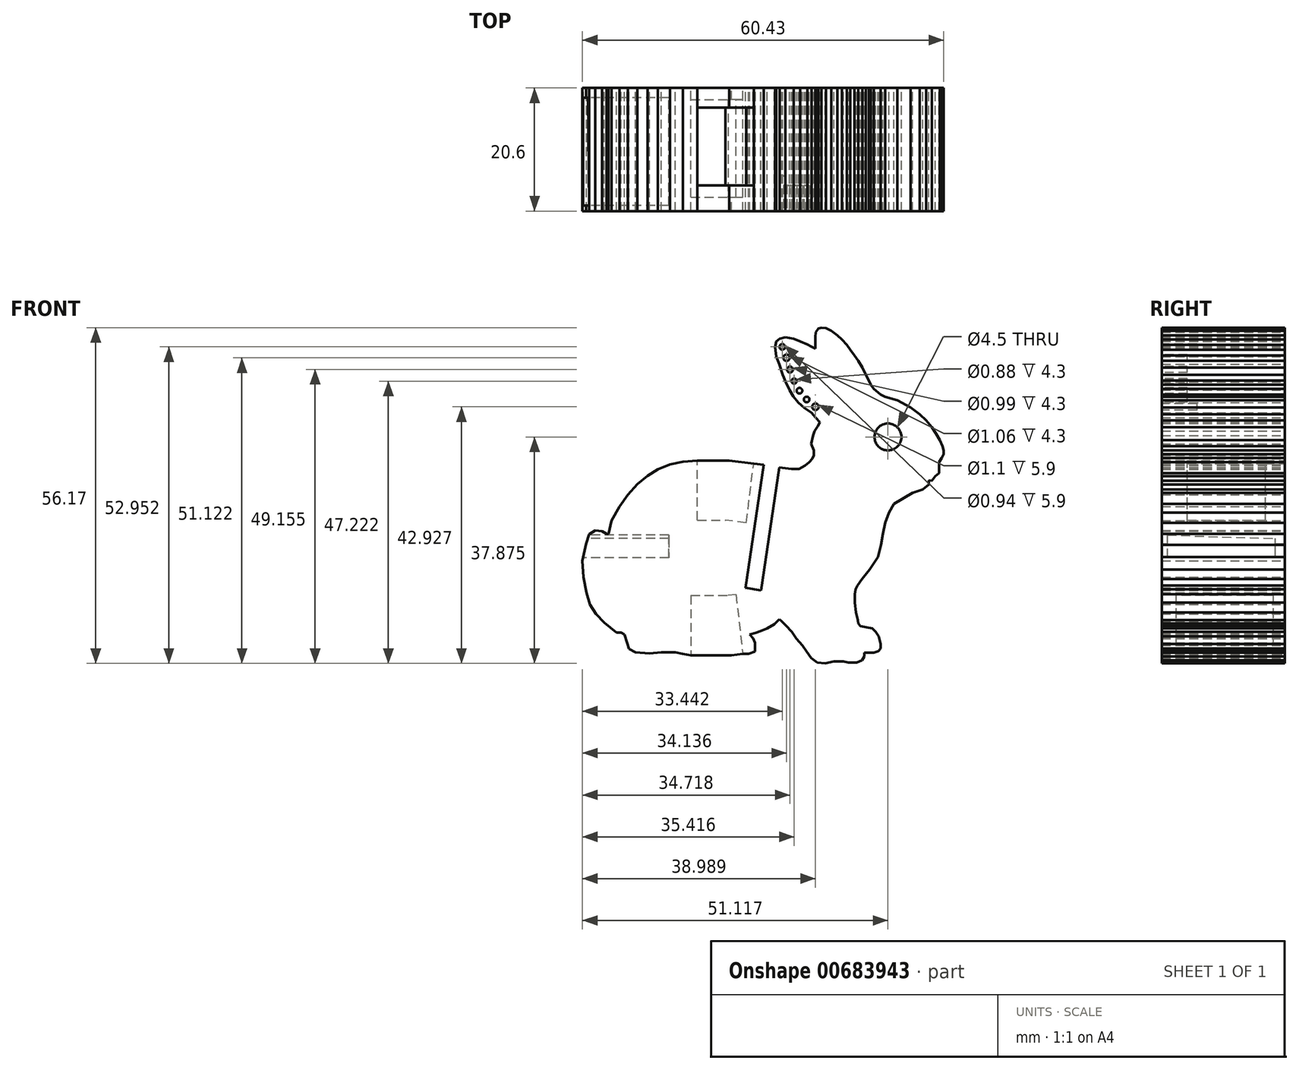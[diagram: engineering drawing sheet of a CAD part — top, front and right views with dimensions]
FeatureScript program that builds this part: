
annotation { "Feature Type Name" : "Feature", "Feature Type Description" : "" }
export const myFeature = defineFeature(function(context is Context, id is Id, definition is map)
    precondition{}
    {
        {
            var Q0;
            Q0=qCreatedBy(makeId("Front.planeOp"),FACE);
            var sketch = newSketch(context, id + "F0", { "sketchPlane" : qUnion([Q0])});
            skLineSegment(sketch, "E0", {"start": v(59.18, 31.9) * mm, "end": v(59.18, 31.2) * mm});
            skLineSegment(sketch, "E1", {"start": v(59.18, 31.2) * mm, "end": v(58.21, 30.37) * mm});
            skLineSegment(sketch, "E2", {"start": v(58.21, 30.37) * mm, "end": v(56.46, 29.85) * mm});
            skLineSegment(sketch, "E3", {"start": v(56.46, 29.85) * mm, "end": v(53.36, 27.96) * mm});
            skLineSegment(sketch, "E4", {"start": v(53.36, 27.96) * mm, "end": v(52.57, 26.52) * mm});
            skLineSegment(sketch, "E5", {"start": v(52.57, 26.52) * mm, "end": v(51.91, 24.8) * mm});
            skLineSegment(sketch, "E6", {"start": v(51.91, 24.8) * mm, "end": v(51.53, 22.99) * mm});
            skLineSegment(sketch, "E7", {"start": v(51.53, 22.99) * mm, "end": v(51.19, 21.11) * mm});
            skLineSegment(sketch, "E8", {"start": v(51.19, 21.11) * mm, "end": v(50.68, 19.1) * mm});
            skLineSegment(sketch, "E9", {"start": v(50.68, 19.1) * mm, "end": v(49.32, 17.01) * mm});
            skLineSegment(sketch, "E10", {"start": v(49.32, 17.01) * mm, "end": v(48.02, 15.39) * mm});
            skLineSegment(sketch, "E11", {"start": v(48.02, 15.39) * mm, "end": v(47.24, 14.33) * mm});
            skLineSegment(sketch, "E12", {"start": v(47.24, 14.33) * mm, "end": v(46.93, 13.71) * mm});
            skLineSegment(sketch, "E13", {"start": v(46.93, 13.71) * mm, "end": v(46.8, 12.88) * mm});
            skLineSegment(sketch, "E14", {"start": v(46.8, 12.88) * mm, "end": v(46.8, 11.49) * mm});
            skLineSegment(sketch, "E15", {"start": v(46.8, 11.49) * mm, "end": v(47.02, 9.82) * mm});
            skLineSegment(sketch, "E16", {"start": v(47.02, 9.82) * mm, "end": v(47.3, 8.54) * mm});
            skLineSegment(sketch, "E17", {"start": v(47.3, 8.54) * mm, "end": v(47.4, 8) * mm});
            skLineSegment(sketch, "E18", {"start": v(47.4, 8) * mm, "end": v(47.8, 7.53) * mm});
            skLineSegment(sketch, "E19", {"start": v(47.8, 7.53) * mm, "end": v(48.73, 7.33) * mm});
            skLineSegment(sketch, "E20", {"start": v(48.73, 7.33) * mm, "end": v(49.72, 7.17) * mm});
            skLineSegment(sketch, "E21", {"start": v(49.72, 7.17) * mm, "end": v(50.33, 6.61) * mm});
            skLineSegment(sketch, "E22", {"start": v(50.33, 6.61) * mm, "end": v(50.85, 5.82) * mm});
            skLineSegment(sketch, "E23", {"start": v(50.85, 5.82) * mm, "end": v(51.16, 4.55) * mm});
            skLineSegment(sketch, "E24", {"start": v(51.16, 4.55) * mm, "end": v(51.16, 3.77) * mm});
            skLineSegment(sketch, "E25", {"start": v(51.16, 3.77) * mm, "end": v(50.77, 3.37) * mm});
            skLineSegment(sketch, "E26", {"start": v(50.77, 3.37) * mm, "end": v(49.97, 3.1) * mm});
            skLineSegment(sketch, "E27", {"start": v(49.97, 3.1) * mm, "end": v(48.4, 3.1) * mm});
            skLineSegment(sketch, "E28", {"start": v(48.4, 3.1) * mm, "end": v(48.4, 2.43) * mm});
            skLineSegment(sketch, "E29", {"start": v(48.4, 2.43) * mm, "end": v(48.04, 1.82) * mm});
            skLineSegment(sketch, "E30", {"start": v(48.04, 1.82) * mm, "end": v(47.14, 1.41) * mm});
            skLineSegment(sketch, "E31", {"start": v(47.14, 1.41) * mm, "end": v(45.74, 1.41) * mm});
            skLineSegment(sketch, "E32", {"start": v(45.74, 1.41) * mm, "end": v(44.91, 1.62) * mm});
            skLineSegment(sketch, "E33", {"start": v(44.91, 1.62) * mm, "end": v(43.35, 1.62) * mm});
            skLineSegment(sketch, "E34", {"start": v(43.35, 1.62) * mm, "end": v(41.85, 1.3) * mm});
            skLineSegment(sketch, "E35", {"start": v(41.85, 1.3) * mm, "end": v(40.56, 1.41) * mm});
            skLineSegment(sketch, "E36", {"start": v(40.56, 1.41) * mm, "end": v(39.54, 2.2) * mm});
            skLineSegment(sketch, "E37", {"start": v(39.54, 2.2) * mm, "end": v(38.77, 3.29) * mm});
            skLineSegment(sketch, "E38", {"start": v(38.77, 3.29) * mm, "end": v(38.07, 4.3) * mm});
            skLineSegment(sketch, "E39", {"start": v(38.07, 4.3) * mm, "end": v(37.07, 5.46) * mm});
            skLineSegment(sketch, "E40", {"start": v(37.07, 5.46) * mm, "end": v(36.3, 6.57) * mm});
            skLineSegment(sketch, "E41", {"start": v(36.3, 6.57) * mm, "end": v(35.28, 7.7) * mm});
            skLineSegment(sketch, "E42", {"start": v(35.28, 7.7) * mm, "end": v(34.6, 8.39) * mm});
            skLineSegment(sketch, "E43", {"start": v(34.6, 8.39) * mm, "end": v(34.18, 8.68) * mm});
            skLineSegment(sketch, "E44", {"start": v(34.18, 8.68) * mm, "end": v(33.34, 7.84) * mm});
            skLineSegment(sketch, "E45", {"start": v(33.34, 7.84) * mm, "end": v(32.19, 7.18) * mm});
            skLineSegment(sketch, "E46", {"start": v(32.19, 7.18) * mm, "end": v(31.1, 6.72) * mm});
            skLineSegment(sketch, "E47", {"start": v(31.1, 6.72) * mm, "end": v(30.18, 6.39) * mm});
            skLineSegment(sketch, "E48", {"start": v(30.18, 6.39) * mm, "end": v(29.26, 6.12) * mm});
            skLineSegment(sketch, "E49", {"start": v(29.26, 6.12) * mm, "end": v(29.8, 5.51) * mm});
            skLineSegment(sketch, "E50", {"start": v(29.8, 5.51) * mm, "end": v(30.13, 4.73) * mm});
            skLineSegment(sketch, "E51", {"start": v(30.13, 4.73) * mm, "end": v(30.13, 4.07) * mm});
            skLineSegment(sketch, "E52", {"start": v(30.13, 4.07) * mm, "end": v(30.13, 3.51) * mm});
            skLineSegment(sketch, "E53", {"start": v(30.13, 3.51) * mm, "end": v(30.13, 3.29) * mm});
            skLineSegment(sketch, "E54", {"start": v(30.13, 3.29) * mm, "end": v(29.07, 2.88) * mm});
            skLineSegment(sketch, "E55", {"start": v(29.07, 2.88) * mm, "end": v(28.07, 2.88) * mm});
            skLineSegment(sketch, "E56", {"start": v(28.07, 2.88) * mm, "end": v(26.19, 2.66) * mm});
            skLineSegment(sketch, "E57", {"start": v(26.19, 2.66) * mm, "end": v(23.74, 2.66) * mm});
            skLineSegment(sketch, "E58", {"start": v(23.74, 2.66) * mm, "end": v(21.88, 2.66) * mm});
            skLineSegment(sketch, "E59", {"start": v(21.88, 2.66) * mm, "end": v(19.4, 2.66) * mm});
            skLineSegment(sketch, "E60", {"start": v(19.4, 2.66) * mm, "end": v(18, 2.88) * mm});
            skLineSegment(sketch, "E61", {"start": v(18, 2.88) * mm, "end": v(16.82, 3.14) * mm});
            skLineSegment(sketch, "E62", {"start": v(16.82, 3.14) * mm, "end": v(14.45, 3.14) * mm});
            skLineSegment(sketch, "E63", {"start": v(14.45, 3.14) * mm, "end": v(12.45, 3) * mm});
            skLineSegment(sketch, "E64", {"start": v(12.45, 3) * mm, "end": v(10.14, 3.13) * mm});
            skLineSegment(sketch, "E65", {"start": v(10.14, 3.13) * mm, "end": v(9.06, 3.73) * mm});
            skLineSegment(sketch, "E66", {"start": v(9.06, 3.73) * mm, "end": v(8.7, 4.73) * mm});
            skLineSegment(sketch, "E67", {"start": v(8.7, 4.73) * mm, "end": v(8.3, 6.14) * mm});
            skLineSegment(sketch, "E68", {"start": v(8.3, 6.14) * mm, "end": v(7.74, 6.47) * mm});
            skLineSegment(sketch, "E69", {"start": v(7.74, 6.47) * mm, "end": v(6.93, 6.47) * mm});
            skLineSegment(sketch, "E70", {"start": v(6.93, 6.47) * mm, "end": v(4.9, 8.14) * mm});
            skLineSegment(sketch, "E71", {"start": v(4.9, 8.14) * mm, "end": v(3.53, 9.54) * mm});
            skLineSegment(sketch, "E72", {"start": v(3.53, 9.54) * mm, "end": v(2.47, 11.15) * mm});
            skLineSegment(sketch, "E73", {"start": v(2.47, 11.15) * mm, "end": v(1.9, 13.14) * mm});
            skLineSegment(sketch, "E74", {"start": v(1.9, 13.14) * mm, "end": v(1.4, 15.75) * mm});
            skLineSegment(sketch, "E75", {"start": v(1.4, 15.75) * mm, "end": v(1.25, 18.43) * mm});
            skLineSegment(sketch, "E76", {"start": v(1.25, 18.43) * mm, "end": v(1.86, 21.3) * mm});
            skLineSegment(sketch, "E77", {"start": v(1.86, 21.3) * mm, "end": v(2.39, 22.87) * mm});
            skLineSegment(sketch, "E78", {"start": v(2.39, 22.87) * mm, "end": v(3.37, 23.56) * mm});
            skLineSegment(sketch, "E79", {"start": v(3.37, 23.56) * mm, "end": v(4.55, 23.4) * mm});
            skLineSegment(sketch, "E80", {"start": v(4.55, 23.4) * mm, "end": v(5.28, 22.99) * mm});
            skLineSegment(sketch, "E81", {"start": v(5.28, 22.99) * mm, "end": v(5.63, 22.99) * mm});
            skLineSegment(sketch, "E82", {"start": v(5.63, 22.99) * mm, "end": v(6.1, 25.22) * mm});
            skLineSegment(sketch, "E83", {"start": v(6.1, 25.22) * mm, "end": v(7.44, 27.53) * mm});
            skLineSegment(sketch, "E84", {"start": v(7.44, 27.53) * mm, "end": v(8.84, 29.53) * mm});
            skLineSegment(sketch, "E85", {"start": v(8.84, 29.53) * mm, "end": v(10.46, 31.27) * mm});
            skLineSegment(sketch, "E86", {"start": v(10.46, 31.27) * mm, "end": v(12.13, 32.66) * mm});
            skLineSegment(sketch, "E87", {"start": v(12.13, 32.66) * mm, "end": v(13.85, 33.74) * mm});
            skLineSegment(sketch, "E88", {"start": v(13.85, 33.74) * mm, "end": v(15.89, 34.56) * mm});
            skLineSegment(sketch, "E89", {"start": v(15.89, 34.56) * mm, "end": v(18.07, 35.02) * mm});
            skLineSegment(sketch, "E90", {"start": v(18.07, 35.02) * mm, "end": v(20.5, 35.25) * mm});
            skLineSegment(sketch, "E91", {"start": v(20.5, 35.25) * mm, "end": v(22.93, 35.25) * mm});
            skLineSegment(sketch, "E92", {"start": v(22.93, 35.25) * mm, "end": v(25.8, 35.25) * mm});
            skLineSegment(sketch, "E93", {"start": v(25.8, 35.25) * mm, "end": v(29.9, 34.74) * mm});
            skLineSegment(sketch, "E94", {"start": v(29.9, 34.74) * mm, "end": v(31.58, 34.5) * mm});
            skLineSegment(sketch, "E95", {"start": v(31.58, 34.5) * mm, "end": v(34.17, 34.11) * mm});
            skLineSegment(sketch, "E96", {"start": v(34.17, 34.11) * mm, "end": v(36.24, 33.84) * mm});
            skLineSegment(sketch, "E97", {"start": v(36.24, 33.84) * mm, "end": v(37.5, 33.84) * mm});
            skLineSegment(sketch, "E98", {"start": v(37.5, 33.84) * mm, "end": v(38.48, 34.41) * mm});
            skLineSegment(sketch, "E99", {"start": v(38.48, 34.41) * mm, "end": v(39.21, 34.95) * mm});
            skLineSegment(sketch, "E100", {"start": v(39.21, 34.95) * mm, "end": v(39.69, 35.51) * mm});
            skLineSegment(sketch, "E101", {"start": v(39.69, 35.51) * mm, "end": v(39.94, 36.1) * mm});
            skLineSegment(sketch, "E102", {"start": v(39.94, 36.1) * mm, "end": v(39.94, 36.93) * mm});
            skLineSegment(sketch, "E103", {"start": v(39.94, 36.93) * mm, "end": v(39.54, 38.02) * mm});
            skLineSegment(sketch, "E104", {"start": v(39.54, 38.02) * mm, "end": v(39.83, 39.44) * mm});
            skLineSegment(sketch, "E105", {"start": v(39.83, 39.44) * mm, "end": v(40.08, 40.2) * mm});
            skLineSegment(sketch, "E106", {"start": v(40.08, 40.2) * mm, "end": v(40.6, 40.94) * mm});
            skLineSegment(sketch, "E107", {"start": v(40.6, 40.94) * mm, "end": v(41, 41.61) * mm});
            skLineSegment(sketch, "E108", {"start": v(41, 41.61) * mm, "end": v(40.3, 42.4) * mm});
            skLineSegment(sketch, "E109", {"start": v(40.3, 42.4) * mm, "end": v(39.57, 43.22) * mm});
            skLineSegment(sketch, "E110", {"start": v(39.57, 43.22) * mm, "end": v(38.4, 44.03) * mm});
            skLineSegment(sketch, "E111", {"start": v(38.4, 44.03) * mm, "end": v(37.38, 44.92) * mm});
            skLineSegment(sketch, "E112", {"start": v(37.38, 44.92) * mm, "end": v(36.53, 45.97) * mm});
            skLineSegment(sketch, "E113", {"start": v(36.53, 45.97) * mm, "end": v(35.9, 47.05) * mm});
            skLineSegment(sketch, "E114", {"start": v(35.9, 47.05) * mm, "end": v(35.26, 48.39) * mm});
            skLineSegment(sketch, "E115", {"start": v(35.26, 48.39) * mm, "end": v(34.77, 49.59) * mm});
            skLineSegment(sketch, "E116", {"start": v(34.77, 49.59) * mm, "end": v(34.17, 51.34) * mm});
            skLineSegment(sketch, "E117", {"start": v(34.17, 51.34) * mm, "end": v(33.68, 52.6) * mm});
            skLineSegment(sketch, "E118", {"start": v(33.68, 52.6) * mm, "end": v(33.5, 54.23) * mm});
            skLineSegment(sketch, "E119", {"start": v(33.5, 54.23) * mm, "end": v(33.67, 55.17) * mm});
            skLineSegment(sketch, "E120", {"start": v(33.67, 55.17) * mm, "end": v(34.28, 55.63) * mm});
            skLineSegment(sketch, "E121", {"start": v(34.28, 55.63) * mm, "end": v(35.19, 55.89) * mm});
            skLineSegment(sketch, "E122", {"start": v(35.19, 55.89) * mm, "end": v(36.57, 55.6) * mm});
            skLineSegment(sketch, "E123", {"start": v(36.57, 55.6) * mm, "end": v(37.7, 55.18) * mm});
            skLineSegment(sketch, "E124", {"start": v(37.7, 55.18) * mm, "end": v(38.87, 54.67) * mm});
            skLineSegment(sketch, "E125", {"start": v(38.87, 54.67) * mm, "end": v(39.6, 54.27) * mm});
            skLineSegment(sketch, "E126", {"start": v(39.6, 54.27) * mm, "end": v(40.2, 53.98) * mm});
            skLineSegment(sketch, "E127", {"start": v(40.2, 53.98) * mm, "end": v(40.2, 55.95) * mm});
            skLineSegment(sketch, "E128", {"start": v(40.2, 55.95) * mm, "end": v(40.3, 56.68) * mm});
            skLineSegment(sketch, "E129", {"start": v(40.3, 56.68) * mm, "end": v(40.7, 57.32) * mm});
            skLineSegment(sketch, "E130", {"start": v(40.7, 57.32) * mm, "end": v(41.2, 57.47) * mm});
            skLineSegment(sketch, "E131", {"start": v(41.2, 57.47) * mm, "end": v(41.98, 57.38) * mm});
            skLineSegment(sketch, "E132", {"start": v(41.98, 57.38) * mm, "end": v(42.9, 56.96) * mm});
            skLineSegment(sketch, "E133", {"start": v(42.9, 56.96) * mm, "end": v(43.88, 56.18) * mm});
            skLineSegment(sketch, "E134", {"start": v(43.88, 56.18) * mm, "end": v(44.66, 55.47) * mm});
            skLineSegment(sketch, "E135", {"start": v(44.66, 55.47) * mm, "end": v(45.46, 54.57) * mm});
            skLineSegment(sketch, "E136", {"start": v(45.46, 54.57) * mm, "end": v(46.07, 53.8) * mm});
            skLineSegment(sketch, "E137", {"start": v(46.07, 53.8) * mm, "end": v(46.74, 52.83) * mm});
            skLineSegment(sketch, "E138", {"start": v(46.74, 52.83) * mm, "end": v(47.4, 51.92) * mm});
            skLineSegment(sketch, "E139", {"start": v(47.4, 51.92) * mm, "end": v(48.07, 50.76) * mm});
            skLineSegment(sketch, "E140", {"start": v(48.07, 50.76) * mm, "end": v(48.69, 49.58) * mm});
            skLineSegment(sketch, "E141", {"start": v(48.69, 49.58) * mm, "end": v(49.16, 48.64) * mm});
            skLineSegment(sketch, "E142", {"start": v(49.16, 48.64) * mm, "end": v(49.5, 47.92) * mm});
            skLineSegment(sketch, "E143", {"start": v(49.5, 47.92) * mm, "end": v(50.03, 47.25) * mm});
            skLineSegment(sketch, "E144", {"start": v(50.03, 47.25) * mm, "end": v(51.16, 46.28) * mm});
            skLineSegment(sketch, "E145", {"start": v(51.16, 46.28) * mm, "end": v(51.87, 45.89) * mm});
            skLineSegment(sketch, "E146", {"start": v(51.87, 45.89) * mm, "end": v(53.94, 45.3) * mm});
            skLineSegment(sketch, "E147", {"start": v(53.94, 45.3) * mm, "end": v(56.13, 44.1) * mm});
            skLineSegment(sketch, "E148", {"start": v(56.13, 44.1) * mm, "end": v(57.69, 42.96) * mm});
            skLineSegment(sketch, "E149", {"start": v(57.69, 42.96) * mm, "end": v(58.76, 41.92) * mm});
            skLineSegment(sketch, "E150", {"start": v(58.76, 41.92) * mm, "end": v(59.7, 40.84) * mm});
            skLineSegment(sketch, "E151", {"start": v(59.7, 40.84) * mm, "end": v(60.39, 39.73) * mm});
            skLineSegment(sketch, "E152", {"start": v(60.39, 39.73) * mm, "end": v(61.06, 38.64) * mm});
            skLineSegment(sketch, "E153", {"start": v(61.06, 38.64) * mm, "end": v(61.48, 37.65) * mm});
            skLineSegment(sketch, "E154", {"start": v(61.48, 37.65) * mm, "end": v(61.68, 36.96) * mm});
            skLineSegment(sketch, "E155", {"start": v(61.68, 36.96) * mm, "end": v(61.68, 36.3) * mm});
            skLineSegment(sketch, "E156", {"start": v(61.68, 36.3) * mm, "end": v(61.36, 35.64) * mm});
            skLineSegment(sketch, "E157", {"start": v(61.36, 35.64) * mm, "end": v(60.9, 34.95) * mm});
            skLineSegment(sketch, "E158", {"start": v(60.9, 34.95) * mm, "end": v(60.9, 33.94) * mm});
            skLineSegment(sketch, "E159", {"start": v(60.9, 33.94) * mm, "end": v(60.9, 33.16) * mm});
            skLineSegment(sketch, "E160", {"start": v(60.9, 33.16) * mm, "end": v(60.3, 32.6) * mm});
            skLineSegment(sketch, "E161", {"start": v(60.3, 32.6) * mm, "end": v(59.74, 31.88) * mm});
            skLineSegment(sketch, "E162", {"start": v(59.74, 31.88) * mm, "end": v(59.18, 31.9) * mm});
            skCircle(sketch, "E163", {"center": v(52.37, 39.17) * mm, "radius": 2.25 * mm});
            skSolve(sketch);
        }
        {
            var Q0;
            Q0=makeQuery(id+"F0.imprint","IMPRINT",FACE,{"disambiguationData":[TD([[makeQuery(id+"F0.imprint","IMPRINT",EDGE,{"derivedFrom":sQuery(id+"F0.wireOp",EDGE,"E0")}),-1.0]])]});
            extrude(context, id + "F1", {"entities" : qUnion([Q0]), "depth" : 3 * mm, "offsetDistance" : 25 * mm});
        }
        {
            var Q0;
            Q0=makeQuery(id+"F1.opExtrude","CAP_FACE",FACE,{"disambiguationData":[OSD([sQuery(id+"F0.wireOp",EDGE,"E0"),sQuery(id+"F0.wireOp",EDGE,"E1"),sQuery(id+"F0.wireOp",EDGE,"E2"),sQuery(id+"F0.wireOp",EDGE,"E3"),sQuery(id+"F0.wireOp",EDGE,"E4"),sQuery(id+"F0.wireOp",EDGE,"E5"),sQuery(id+"F0.wireOp",EDGE,"E6"),sQuery(id+"F0.wireOp",EDGE,"E7"),sQuery(id+"F0.wireOp",EDGE,"E8"),sQuery(id+"F0.wireOp",EDGE,"E9"),sQuery(id+"F0.wireOp",EDGE,"E10"),sQuery(id+"F0.wireOp",EDGE,"E11"),sQuery(id+"F0.wireOp",EDGE,"E12"),sQuery(id+"F0.wireOp",EDGE,"E13"),sQuery(id+"F0.wireOp",EDGE,"E14"),sQuery(id+"F0.wireOp",EDGE,"E15"),sQuery(id+"F0.wireOp",EDGE,"E16"),sQuery(id+"F0.wireOp",EDGE,"E17"),sQuery(id+"F0.wireOp",EDGE,"E18"),sQuery(id+"F0.wireOp",EDGE,"E19"),sQuery(id+"F0.wireOp",EDGE,"E20"),sQuery(id+"F0.wireOp",EDGE,"E21"),sQuery(id+"F0.wireOp",EDGE,"E22"),sQuery(id+"F0.wireOp",EDGE,"E23"),sQuery(id+"F0.wireOp",EDGE,"E24"),sQuery(id+"F0.wireOp",EDGE,"E25"),sQuery(id+"F0.wireOp",EDGE,"E26"),sQuery(id+"F0.wireOp",EDGE,"E27"),sQuery(id+"F0.wireOp",EDGE,"E28"),sQuery(id+"F0.wireOp",EDGE,"E29"),sQuery(id+"F0.wireOp",EDGE,"E30"),sQuery(id+"F0.wireOp",EDGE,"E31"),sQuery(id+"F0.wireOp",EDGE,"E32"),sQuery(id+"F0.wireOp",EDGE,"E33"),sQuery(id+"F0.wireOp",EDGE,"E34"),sQuery(id+"F0.wireOp",EDGE,"E35"),sQuery(id+"F0.wireOp",EDGE,"E36"),sQuery(id+"F0.wireOp",EDGE,"E37"),sQuery(id+"F0.wireOp",EDGE,"E38"),sQuery(id+"F0.wireOp",EDGE,"E39"),sQuery(id+"F0.wireOp",EDGE,"E40"),sQuery(id+"F0.wireOp",EDGE,"E41"),sQuery(id+"F0.wireOp",EDGE,"E42"),sQuery(id+"F0.wireOp",EDGE,"E43"),sQuery(id+"F0.wireOp",EDGE,"E44"),sQuery(id+"F0.wireOp",EDGE,"E45"),sQuery(id+"F0.wireOp",EDGE,"E46"),sQuery(id+"F0.wireOp",EDGE,"E47"),sQuery(id+"F0.wireOp",EDGE,"E48"),sQuery(id+"F0.wireOp",EDGE,"E49"),sQuery(id+"F0.wireOp",EDGE,"E50"),sQuery(id+"F0.wireOp",EDGE,"E51"),sQuery(id+"F0.wireOp",EDGE,"E52"),sQuery(id+"F0.wireOp",EDGE,"E53"),sQuery(id+"F0.wireOp",EDGE,"E54"),sQuery(id+"F0.wireOp",EDGE,"E55"),sQuery(id+"F0.wireOp",EDGE,"E56"),sQuery(id+"F0.wireOp",EDGE,"E57"),sQuery(id+"F0.wireOp",EDGE,"E58"),sQuery(id+"F0.wireOp",EDGE,"E59"),sQuery(id+"F0.wireOp",EDGE,"E60"),sQuery(id+"F0.wireOp",EDGE,"E61"),sQuery(id+"F0.wireOp",EDGE,"E62"),sQuery(id+"F0.wireOp",EDGE,"E63"),sQuery(id+"F0.wireOp",EDGE,"E64"),sQuery(id+"F0.wireOp",EDGE,"E65"),sQuery(id+"F0.wireOp",EDGE,"E66"),sQuery(id+"F0.wireOp",EDGE,"E67"),sQuery(id+"F0.wireOp",EDGE,"E68"),sQuery(id+"F0.wireOp",EDGE,"E69"),sQuery(id+"F0.wireOp",EDGE,"E70"),sQuery(id+"F0.wireOp",EDGE,"E71"),sQuery(id+"F0.wireOp",EDGE,"E72"),sQuery(id+"F0.wireOp",EDGE,"E73"),sQuery(id+"F0.wireOp",EDGE,"E74"),sQuery(id+"F0.wireOp",EDGE,"E75"),sQuery(id+"F0.wireOp",EDGE,"E76"),sQuery(id+"F0.wireOp",EDGE,"E77"),sQuery(id+"F0.wireOp",EDGE,"E78"),sQuery(id+"F0.wireOp",EDGE,"E79"),sQuery(id+"F0.wireOp",EDGE,"E80"),sQuery(id+"F0.wireOp",EDGE,"E81"),sQuery(id+"F0.wireOp",EDGE,"E82"),sQuery(id+"F0.wireOp",EDGE,"E83"),sQuery(id+"F0.wireOp",EDGE,"E84"),sQuery(id+"F0.wireOp",EDGE,"E85"),sQuery(id+"F0.wireOp",EDGE,"E86"),sQuery(id+"F0.wireOp",EDGE,"E87"),sQuery(id+"F0.wireOp",EDGE,"E88"),sQuery(id+"F0.wireOp",EDGE,"E89"),sQuery(id+"F0.wireOp",EDGE,"E90"),sQuery(id+"F0.wireOp",EDGE,"E91"),sQuery(id+"F0.wireOp",EDGE,"E92"),sQuery(id+"F0.wireOp",EDGE,"E93"),sQuery(id+"F0.wireOp",EDGE,"E94"),sQuery(id+"F0.wireOp",EDGE,"E95"),sQuery(id+"F0.wireOp",EDGE,"E96"),sQuery(id+"F0.wireOp",EDGE,"E97"),sQuery(id+"F0.wireOp",EDGE,"E98"),sQuery(id+"F0.wireOp",EDGE,"E99"),sQuery(id+"F0.wireOp",EDGE,"E100"),sQuery(id+"F0.wireOp",EDGE,"E101"),sQuery(id+"F0.wireOp",EDGE,"E102"),sQuery(id+"F0.wireOp",EDGE,"E103"),sQuery(id+"F0.wireOp",EDGE,"E104"),sQuery(id+"F0.wireOp",EDGE,"E105"),sQuery(id+"F0.wireOp",EDGE,"E106"),sQuery(id+"F0.wireOp",EDGE,"E107"),sQuery(id+"F0.wireOp",EDGE,"E108"),sQuery(id+"F0.wireOp",EDGE,"E109"),sQuery(id+"F0.wireOp",EDGE,"E110"),sQuery(id+"F0.wireOp",EDGE,"E111"),sQuery(id+"F0.wireOp",EDGE,"E112"),sQuery(id+"F0.wireOp",EDGE,"E113"),sQuery(id+"F0.wireOp",EDGE,"E114"),sQuery(id+"F0.wireOp",EDGE,"E115"),sQuery(id+"F0.wireOp",EDGE,"E116"),sQuery(id+"F0.wireOp",EDGE,"E117"),sQuery(id+"F0.wireOp",EDGE,"E118"),sQuery(id+"F0.wireOp",EDGE,"E119"),sQuery(id+"F0.wireOp",EDGE,"E120"),sQuery(id+"F0.wireOp",EDGE,"E121"),sQuery(id+"F0.wireOp",EDGE,"E122"),sQuery(id+"F0.wireOp",EDGE,"E123"),sQuery(id+"F0.wireOp",EDGE,"E124"),sQuery(id+"F0.wireOp",EDGE,"E125"),sQuery(id+"F0.wireOp",EDGE,"E126"),sQuery(id+"F0.wireOp",EDGE,"E127"),sQuery(id+"F0.wireOp",EDGE,"E128"),sQuery(id+"F0.wireOp",EDGE,"E129"),sQuery(id+"F0.wireOp",EDGE,"E130"),sQuery(id+"F0.wireOp",EDGE,"E131"),sQuery(id+"F0.wireOp",EDGE,"E132"),sQuery(id+"F0.wireOp",EDGE,"E133"),sQuery(id+"F0.wireOp",EDGE,"E134"),sQuery(id+"F0.wireOp",EDGE,"E135"),sQuery(id+"F0.wireOp",EDGE,"E136"),sQuery(id+"F0.wireOp",EDGE,"E137"),sQuery(id+"F0.wireOp",EDGE,"E138"),sQuery(id+"F0.wireOp",EDGE,"E139"),sQuery(id+"F0.wireOp",EDGE,"E140"),sQuery(id+"F0.wireOp",EDGE,"E141"),sQuery(id+"F0.wireOp",EDGE,"E142"),sQuery(id+"F0.wireOp",EDGE,"E143"),sQuery(id+"F0.wireOp",EDGE,"E144"),sQuery(id+"F0.wireOp",EDGE,"E145"),sQuery(id+"F0.wireOp",EDGE,"E146"),sQuery(id+"F0.wireOp",EDGE,"E147"),sQuery(id+"F0.wireOp",EDGE,"E148"),sQuery(id+"F0.wireOp",EDGE,"E149"),sQuery(id+"F0.wireOp",EDGE,"E150"),sQuery(id+"F0.wireOp",EDGE,"E151"),sQuery(id+"F0.wireOp",EDGE,"E152"),sQuery(id+"F0.wireOp",EDGE,"E153"),sQuery(id+"F0.wireOp",EDGE,"E154"),sQuery(id+"F0.wireOp",EDGE,"E155"),sQuery(id+"F0.wireOp",EDGE,"E156"),sQuery(id+"F0.wireOp",EDGE,"E157"),sQuery(id+"F0.wireOp",EDGE,"E158"),sQuery(id+"F0.wireOp",EDGE,"E159"),sQuery(id+"F0.wireOp",EDGE,"E160"),sQuery(id+"F0.wireOp",EDGE,"E161"),sQuery(id+"F0.wireOp",EDGE,"E162"),sQuery(id+"F0.wireOp",EDGE,"E163")])],"isStart":false});
            extrude(context, id + "F2", {"entities" : qUnion([Q0]), "operationType" : NewBodyOperationType.ADD, "depth" : 17.6 * mm, "offsetDistance" : 25 * mm});
        }
        {
            var Q0;
            Q0=makeQuery(id+"F2.opExtrude","CAP_FACE",FACE,{"disambiguationData":[OSD([sQuery(id+"F0.wireOp",EDGE,"E0"),sQuery(id+"F0.wireOp",EDGE,"E1"),sQuery(id+"F0.wireOp",EDGE,"E2"),sQuery(id+"F0.wireOp",EDGE,"E3"),sQuery(id+"F0.wireOp",EDGE,"E4"),sQuery(id+"F0.wireOp",EDGE,"E5"),sQuery(id+"F0.wireOp",EDGE,"E6"),sQuery(id+"F0.wireOp",EDGE,"E7"),sQuery(id+"F0.wireOp",EDGE,"E8"),sQuery(id+"F0.wireOp",EDGE,"E9"),sQuery(id+"F0.wireOp",EDGE,"E10"),sQuery(id+"F0.wireOp",EDGE,"E11"),sQuery(id+"F0.wireOp",EDGE,"E12"),sQuery(id+"F0.wireOp",EDGE,"E13"),sQuery(id+"F0.wireOp",EDGE,"E14"),sQuery(id+"F0.wireOp",EDGE,"E15"),sQuery(id+"F0.wireOp",EDGE,"E16"),sQuery(id+"F0.wireOp",EDGE,"E17"),sQuery(id+"F0.wireOp",EDGE,"E18"),sQuery(id+"F0.wireOp",EDGE,"E19"),sQuery(id+"F0.wireOp",EDGE,"E20"),sQuery(id+"F0.wireOp",EDGE,"E21"),sQuery(id+"F0.wireOp",EDGE,"E22"),sQuery(id+"F0.wireOp",EDGE,"E23"),sQuery(id+"F0.wireOp",EDGE,"E24"),sQuery(id+"F0.wireOp",EDGE,"E25"),sQuery(id+"F0.wireOp",EDGE,"E26"),sQuery(id+"F0.wireOp",EDGE,"E27"),sQuery(id+"F0.wireOp",EDGE,"E28"),sQuery(id+"F0.wireOp",EDGE,"E29"),sQuery(id+"F0.wireOp",EDGE,"E30"),sQuery(id+"F0.wireOp",EDGE,"E31"),sQuery(id+"F0.wireOp",EDGE,"E32"),sQuery(id+"F0.wireOp",EDGE,"E33"),sQuery(id+"F0.wireOp",EDGE,"E34"),sQuery(id+"F0.wireOp",EDGE,"E35"),sQuery(id+"F0.wireOp",EDGE,"E36"),sQuery(id+"F0.wireOp",EDGE,"E37"),sQuery(id+"F0.wireOp",EDGE,"E38"),sQuery(id+"F0.wireOp",EDGE,"E39"),sQuery(id+"F0.wireOp",EDGE,"E40"),sQuery(id+"F0.wireOp",EDGE,"E41"),sQuery(id+"F0.wireOp",EDGE,"E42"),sQuery(id+"F0.wireOp",EDGE,"E43"),sQuery(id+"F0.wireOp",EDGE,"E44"),sQuery(id+"F0.wireOp",EDGE,"E45"),sQuery(id+"F0.wireOp",EDGE,"E46"),sQuery(id+"F0.wireOp",EDGE,"E47"),sQuery(id+"F0.wireOp",EDGE,"E48"),sQuery(id+"F0.wireOp",EDGE,"E49"),sQuery(id+"F0.wireOp",EDGE,"E50"),sQuery(id+"F0.wireOp",EDGE,"E51"),sQuery(id+"F0.wireOp",EDGE,"E52"),sQuery(id+"F0.wireOp",EDGE,"E53"),sQuery(id+"F0.wireOp",EDGE,"E54"),sQuery(id+"F0.wireOp",EDGE,"E55"),sQuery(id+"F0.wireOp",EDGE,"E56"),sQuery(id+"F0.wireOp",EDGE,"E57"),sQuery(id+"F0.wireOp",EDGE,"E58"),sQuery(id+"F0.wireOp",EDGE,"E59"),sQuery(id+"F0.wireOp",EDGE,"E60"),sQuery(id+"F0.wireOp",EDGE,"E61"),sQuery(id+"F0.wireOp",EDGE,"E62"),sQuery(id+"F0.wireOp",EDGE,"E63"),sQuery(id+"F0.wireOp",EDGE,"E64"),sQuery(id+"F0.wireOp",EDGE,"E65"),sQuery(id+"F0.wireOp",EDGE,"E66"),sQuery(id+"F0.wireOp",EDGE,"E67"),sQuery(id+"F0.wireOp",EDGE,"E68"),sQuery(id+"F0.wireOp",EDGE,"E69"),sQuery(id+"F0.wireOp",EDGE,"E70"),sQuery(id+"F0.wireOp",EDGE,"E71"),sQuery(id+"F0.wireOp",EDGE,"E72"),sQuery(id+"F0.wireOp",EDGE,"E73"),sQuery(id+"F0.wireOp",EDGE,"E74"),sQuery(id+"F0.wireOp",EDGE,"E75"),sQuery(id+"F0.wireOp",EDGE,"E76"),sQuery(id+"F0.wireOp",EDGE,"E77"),sQuery(id+"F0.wireOp",EDGE,"E78"),sQuery(id+"F0.wireOp",EDGE,"E79"),sQuery(id+"F0.wireOp",EDGE,"E80"),sQuery(id+"F0.wireOp",EDGE,"E81"),sQuery(id+"F0.wireOp",EDGE,"E82"),sQuery(id+"F0.wireOp",EDGE,"E83"),sQuery(id+"F0.wireOp",EDGE,"E84"),sQuery(id+"F0.wireOp",EDGE,"E85"),sQuery(id+"F0.wireOp",EDGE,"E86"),sQuery(id+"F0.wireOp",EDGE,"E87"),sQuery(id+"F0.wireOp",EDGE,"E88"),sQuery(id+"F0.wireOp",EDGE,"E89"),sQuery(id+"F0.wireOp",EDGE,"E90"),sQuery(id+"F0.wireOp",EDGE,"E91"),sQuery(id+"F0.wireOp",EDGE,"E92"),sQuery(id+"F0.wireOp",EDGE,"E93"),sQuery(id+"F0.wireOp",EDGE,"E94"),sQuery(id+"F0.wireOp",EDGE,"E95"),sQuery(id+"F0.wireOp",EDGE,"E96"),sQuery(id+"F0.wireOp",EDGE,"E97"),sQuery(id+"F0.wireOp",EDGE,"E98"),sQuery(id+"F0.wireOp",EDGE,"E99"),sQuery(id+"F0.wireOp",EDGE,"E100"),sQuery(id+"F0.wireOp",EDGE,"E101"),sQuery(id+"F0.wireOp",EDGE,"E102"),sQuery(id+"F0.wireOp",EDGE,"E103"),sQuery(id+"F0.wireOp",EDGE,"E104"),sQuery(id+"F0.wireOp",EDGE,"E105"),sQuery(id+"F0.wireOp",EDGE,"E106"),sQuery(id+"F0.wireOp",EDGE,"E107"),sQuery(id+"F0.wireOp",EDGE,"E108"),sQuery(id+"F0.wireOp",EDGE,"E109"),sQuery(id+"F0.wireOp",EDGE,"E110"),sQuery(id+"F0.wireOp",EDGE,"E111"),sQuery(id+"F0.wireOp",EDGE,"E112"),sQuery(id+"F0.wireOp",EDGE,"E113"),sQuery(id+"F0.wireOp",EDGE,"E114"),sQuery(id+"F0.wireOp",EDGE,"E115"),sQuery(id+"F0.wireOp",EDGE,"E116"),sQuery(id+"F0.wireOp",EDGE,"E117"),sQuery(id+"F0.wireOp",EDGE,"E118"),sQuery(id+"F0.wireOp",EDGE,"E119"),sQuery(id+"F0.wireOp",EDGE,"E120"),sQuery(id+"F0.wireOp",EDGE,"E121"),sQuery(id+"F0.wireOp",EDGE,"E122"),sQuery(id+"F0.wireOp",EDGE,"E123"),sQuery(id+"F0.wireOp",EDGE,"E124"),sQuery(id+"F0.wireOp",EDGE,"E125"),sQuery(id+"F0.wireOp",EDGE,"E126"),sQuery(id+"F0.wireOp",EDGE,"E127"),sQuery(id+"F0.wireOp",EDGE,"E128"),sQuery(id+"F0.wireOp",EDGE,"E129"),sQuery(id+"F0.wireOp",EDGE,"E130"),sQuery(id+"F0.wireOp",EDGE,"E131"),sQuery(id+"F0.wireOp",EDGE,"E132"),sQuery(id+"F0.wireOp",EDGE,"E133"),sQuery(id+"F0.wireOp",EDGE,"E134"),sQuery(id+"F0.wireOp",EDGE,"E135"),sQuery(id+"F0.wireOp",EDGE,"E136"),sQuery(id+"F0.wireOp",EDGE,"E137"),sQuery(id+"F0.wireOp",EDGE,"E138"),sQuery(id+"F0.wireOp",EDGE,"E139"),sQuery(id+"F0.wireOp",EDGE,"E140"),sQuery(id+"F0.wireOp",EDGE,"E141"),sQuery(id+"F0.wireOp",EDGE,"E142"),sQuery(id+"F0.wireOp",EDGE,"E143"),sQuery(id+"F0.wireOp",EDGE,"E144"),sQuery(id+"F0.wireOp",EDGE,"E145"),sQuery(id+"F0.wireOp",EDGE,"E146"),sQuery(id+"F0.wireOp",EDGE,"E147"),sQuery(id+"F0.wireOp",EDGE,"E148"),sQuery(id+"F0.wireOp",EDGE,"E149"),sQuery(id+"F0.wireOp",EDGE,"E150"),sQuery(id+"F0.wireOp",EDGE,"E151"),sQuery(id+"F0.wireOp",EDGE,"E152"),sQuery(id+"F0.wireOp",EDGE,"E153"),sQuery(id+"F0.wireOp",EDGE,"E154"),sQuery(id+"F0.wireOp",EDGE,"E155"),sQuery(id+"F0.wireOp",EDGE,"E156"),sQuery(id+"F0.wireOp",EDGE,"E157"),sQuery(id+"F0.wireOp",EDGE,"E158"),sQuery(id+"F0.wireOp",EDGE,"E159"),sQuery(id+"F0.wireOp",EDGE,"E160"),sQuery(id+"F0.wireOp",EDGE,"E161"),sQuery(id+"F0.wireOp",EDGE,"E162"),sQuery(id+"F0.wireOp",EDGE,"E163")])],"isStart":false});
            var sketch = newSketch(context, id + "F3", { "sketchPlane" : qUnion([Q0])});
            skCircle(sketch, "E164", {"center": v(34.92, 54.3) * mm, "radius": 0.54 * mm});
            skCircle(sketch, "E165", {"center": v(35.39, 52.42) * mm, "radius": 0.53 * mm});
            skCircle(sketch, "E166", {"center": v(35.97, 50.45) * mm, "radius": 0.5 * mm});
            skCircle(sketch, "E167", {"center": v(36.67, 48.52) * mm, "radius": 0.44 * mm});
            skCircle(sketch, "E168", {"center": v(37.56, 46.92) * mm, "radius": 0.47 * mm});
            skCircle(sketch, "E169", {"center": v(38.76, 45.45) * mm, "radius": 0.47 * mm});
            skPoint(sketch, "E169.centerSnap0", {"position": v(36.96, 45.45) * mm});
            skSolve(sketch);
        }
        {
            var Q0;
            Q0=makeQuery(id+"F3.imprint","IMPRINT",FACE,{"disambiguationData":[TD([[makeQuery(id+"F3.imprint","IMPRINT",EDGE,{"derivedFrom":sQuery(id+"F3.wireOp",EDGE,"E165")}),1.0]])]});
            var Q1;
            Q1=makeQuery(id+"F3.imprint","IMPRINT",FACE,{"disambiguationData":[TD([[makeQuery(id+"F3.imprint","IMPRINT",EDGE,{"derivedFrom":sQuery(id+"F3.wireOp",EDGE,"E166")}),1.0]])]});
            var Q2;
            Q2=makeQuery(id+"F3.imprint","IMPRINT",FACE,{"disambiguationData":[TD([[makeQuery(id+"F3.imprint","IMPRINT",EDGE,{"derivedFrom":sQuery(id+"F3.wireOp",EDGE,"E167")}),1.0]])]});
            var Q3;
            Q3=makeQuery(id+"F3.imprint","IMPRINT",FACE,{"disambiguationData":[TD([[makeQuery(id+"F3.imprint","IMPRINT",EDGE,{"derivedFrom":sQuery(id+"F3.wireOp",EDGE,"E168")}),1.0]])]});
            var Q4;
            Q4=makeQuery(id+"F3.imprint","IMPRINT",FACE,{"disambiguationData":[TD([[makeQuery(id+"F3.imprint","IMPRINT",EDGE,{"derivedFrom":sQuery(id+"F3.wireOp",EDGE,"E169")}),1.0]])]});
            extrude(context, id + "F4", {"entities" : qUnion([Q0, Q1, Q2, Q3, Q4]), "operationType" : NewBodyOperationType.REMOVE, "oppositeDirection" : true, "depth" : 4.3 * mm, "offsetDistance" : 25 * mm});
        }
        {
            var Q0;
            Q0=makeQuery(id+"F2.opExtrude","CAP_FACE",FACE,{"disambiguationData":[OSD([sQuery(id+"F0.wireOp",EDGE,"E0"),sQuery(id+"F0.wireOp",EDGE,"E1"),sQuery(id+"F0.wireOp",EDGE,"E2"),sQuery(id+"F0.wireOp",EDGE,"E3"),sQuery(id+"F0.wireOp",EDGE,"E4"),sQuery(id+"F0.wireOp",EDGE,"E5"),sQuery(id+"F0.wireOp",EDGE,"E6"),sQuery(id+"F0.wireOp",EDGE,"E7"),sQuery(id+"F0.wireOp",EDGE,"E8"),sQuery(id+"F0.wireOp",EDGE,"E9"),sQuery(id+"F0.wireOp",EDGE,"E10"),sQuery(id+"F0.wireOp",EDGE,"E11"),sQuery(id+"F0.wireOp",EDGE,"E12"),sQuery(id+"F0.wireOp",EDGE,"E13"),sQuery(id+"F0.wireOp",EDGE,"E14"),sQuery(id+"F0.wireOp",EDGE,"E15"),sQuery(id+"F0.wireOp",EDGE,"E16"),sQuery(id+"F0.wireOp",EDGE,"E17"),sQuery(id+"F0.wireOp",EDGE,"E18"),sQuery(id+"F0.wireOp",EDGE,"E19"),sQuery(id+"F0.wireOp",EDGE,"E20"),sQuery(id+"F0.wireOp",EDGE,"E21"),sQuery(id+"F0.wireOp",EDGE,"E22"),sQuery(id+"F0.wireOp",EDGE,"E23"),sQuery(id+"F0.wireOp",EDGE,"E24"),sQuery(id+"F0.wireOp",EDGE,"E25"),sQuery(id+"F0.wireOp",EDGE,"E26"),sQuery(id+"F0.wireOp",EDGE,"E27"),sQuery(id+"F0.wireOp",EDGE,"E28"),sQuery(id+"F0.wireOp",EDGE,"E29"),sQuery(id+"F0.wireOp",EDGE,"E30"),sQuery(id+"F0.wireOp",EDGE,"E31"),sQuery(id+"F0.wireOp",EDGE,"E32"),sQuery(id+"F0.wireOp",EDGE,"E33"),sQuery(id+"F0.wireOp",EDGE,"E34"),sQuery(id+"F0.wireOp",EDGE,"E35"),sQuery(id+"F0.wireOp",EDGE,"E36"),sQuery(id+"F0.wireOp",EDGE,"E37"),sQuery(id+"F0.wireOp",EDGE,"E38"),sQuery(id+"F0.wireOp",EDGE,"E39"),sQuery(id+"F0.wireOp",EDGE,"E40"),sQuery(id+"F0.wireOp",EDGE,"E41"),sQuery(id+"F0.wireOp",EDGE,"E42"),sQuery(id+"F0.wireOp",EDGE,"E43"),sQuery(id+"F0.wireOp",EDGE,"E44"),sQuery(id+"F0.wireOp",EDGE,"E45"),sQuery(id+"F0.wireOp",EDGE,"E46"),sQuery(id+"F0.wireOp",EDGE,"E47"),sQuery(id+"F0.wireOp",EDGE,"E48"),sQuery(id+"F0.wireOp",EDGE,"E49"),sQuery(id+"F0.wireOp",EDGE,"E50"),sQuery(id+"F0.wireOp",EDGE,"E51"),sQuery(id+"F0.wireOp",EDGE,"E52"),sQuery(id+"F0.wireOp",EDGE,"E53"),sQuery(id+"F0.wireOp",EDGE,"E54"),sQuery(id+"F0.wireOp",EDGE,"E55"),sQuery(id+"F0.wireOp",EDGE,"E56"),sQuery(id+"F0.wireOp",EDGE,"E57"),sQuery(id+"F0.wireOp",EDGE,"E58"),sQuery(id+"F0.wireOp",EDGE,"E59"),sQuery(id+"F0.wireOp",EDGE,"E60"),sQuery(id+"F0.wireOp",EDGE,"E61"),sQuery(id+"F0.wireOp",EDGE,"E62"),sQuery(id+"F0.wireOp",EDGE,"E63"),sQuery(id+"F0.wireOp",EDGE,"E64"),sQuery(id+"F0.wireOp",EDGE,"E65"),sQuery(id+"F0.wireOp",EDGE,"E66"),sQuery(id+"F0.wireOp",EDGE,"E67"),sQuery(id+"F0.wireOp",EDGE,"E68"),sQuery(id+"F0.wireOp",EDGE,"E69"),sQuery(id+"F0.wireOp",EDGE,"E70"),sQuery(id+"F0.wireOp",EDGE,"E71"),sQuery(id+"F0.wireOp",EDGE,"E72"),sQuery(id+"F0.wireOp",EDGE,"E73"),sQuery(id+"F0.wireOp",EDGE,"E74"),sQuery(id+"F0.wireOp",EDGE,"E75"),sQuery(id+"F0.wireOp",EDGE,"E76"),sQuery(id+"F0.wireOp",EDGE,"E77"),sQuery(id+"F0.wireOp",EDGE,"E78"),sQuery(id+"F0.wireOp",EDGE,"E79"),sQuery(id+"F0.wireOp",EDGE,"E80"),sQuery(id+"F0.wireOp",EDGE,"E81"),sQuery(id+"F0.wireOp",EDGE,"E82"),sQuery(id+"F0.wireOp",EDGE,"E83"),sQuery(id+"F0.wireOp",EDGE,"E84"),sQuery(id+"F0.wireOp",EDGE,"E85"),sQuery(id+"F0.wireOp",EDGE,"E86"),sQuery(id+"F0.wireOp",EDGE,"E87"),sQuery(id+"F0.wireOp",EDGE,"E88"),sQuery(id+"F0.wireOp",EDGE,"E89"),sQuery(id+"F0.wireOp",EDGE,"E90"),sQuery(id+"F0.wireOp",EDGE,"E91"),sQuery(id+"F0.wireOp",EDGE,"E92"),sQuery(id+"F0.wireOp",EDGE,"E93"),sQuery(id+"F0.wireOp",EDGE,"E94"),sQuery(id+"F0.wireOp",EDGE,"E95"),sQuery(id+"F0.wireOp",EDGE,"E96"),sQuery(id+"F0.wireOp",EDGE,"E97"),sQuery(id+"F0.wireOp",EDGE,"E98"),sQuery(id+"F0.wireOp",EDGE,"E99"),sQuery(id+"F0.wireOp",EDGE,"E100"),sQuery(id+"F0.wireOp",EDGE,"E101"),sQuery(id+"F0.wireOp",EDGE,"E102"),sQuery(id+"F0.wireOp",EDGE,"E103"),sQuery(id+"F0.wireOp",EDGE,"E104"),sQuery(id+"F0.wireOp",EDGE,"E105"),sQuery(id+"F0.wireOp",EDGE,"E106"),sQuery(id+"F0.wireOp",EDGE,"E107"),sQuery(id+"F0.wireOp",EDGE,"E108"),sQuery(id+"F0.wireOp",EDGE,"E109"),sQuery(id+"F0.wireOp",EDGE,"E110"),sQuery(id+"F0.wireOp",EDGE,"E111"),sQuery(id+"F0.wireOp",EDGE,"E112"),sQuery(id+"F0.wireOp",EDGE,"E113"),sQuery(id+"F0.wireOp",EDGE,"E114"),sQuery(id+"F0.wireOp",EDGE,"E115"),sQuery(id+"F0.wireOp",EDGE,"E116"),sQuery(id+"F0.wireOp",EDGE,"E117"),sQuery(id+"F0.wireOp",EDGE,"E118"),sQuery(id+"F0.wireOp",EDGE,"E119"),sQuery(id+"F0.wireOp",EDGE,"E120"),sQuery(id+"F0.wireOp",EDGE,"E121"),sQuery(id+"F0.wireOp",EDGE,"E122"),sQuery(id+"F0.wireOp",EDGE,"E123"),sQuery(id+"F0.wireOp",EDGE,"E124"),sQuery(id+"F0.wireOp",EDGE,"E125"),sQuery(id+"F0.wireOp",EDGE,"E126"),sQuery(id+"F0.wireOp",EDGE,"E127"),sQuery(id+"F0.wireOp",EDGE,"E128"),sQuery(id+"F0.wireOp",EDGE,"E129"),sQuery(id+"F0.wireOp",EDGE,"E130"),sQuery(id+"F0.wireOp",EDGE,"E131"),sQuery(id+"F0.wireOp",EDGE,"E132"),sQuery(id+"F0.wireOp",EDGE,"E133"),sQuery(id+"F0.wireOp",EDGE,"E134"),sQuery(id+"F0.wireOp",EDGE,"E135"),sQuery(id+"F0.wireOp",EDGE,"E136"),sQuery(id+"F0.wireOp",EDGE,"E137"),sQuery(id+"F0.wireOp",EDGE,"E138"),sQuery(id+"F0.wireOp",EDGE,"E139"),sQuery(id+"F0.wireOp",EDGE,"E140"),sQuery(id+"F0.wireOp",EDGE,"E141"),sQuery(id+"F0.wireOp",EDGE,"E142"),sQuery(id+"F0.wireOp",EDGE,"E143"),sQuery(id+"F0.wireOp",EDGE,"E144"),sQuery(id+"F0.wireOp",EDGE,"E145"),sQuery(id+"F0.wireOp",EDGE,"E146"),sQuery(id+"F0.wireOp",EDGE,"E147"),sQuery(id+"F0.wireOp",EDGE,"E148"),sQuery(id+"F0.wireOp",EDGE,"E149"),sQuery(id+"F0.wireOp",EDGE,"E150"),sQuery(id+"F0.wireOp",EDGE,"E151"),sQuery(id+"F0.wireOp",EDGE,"E152"),sQuery(id+"F0.wireOp",EDGE,"E153"),sQuery(id+"F0.wireOp",EDGE,"E154"),sQuery(id+"F0.wireOp",EDGE,"E155"),sQuery(id+"F0.wireOp",EDGE,"E156"),sQuery(id+"F0.wireOp",EDGE,"E157"),sQuery(id+"F0.wireOp",EDGE,"E158"),sQuery(id+"F0.wireOp",EDGE,"E159"),sQuery(id+"F0.wireOp",EDGE,"E160"),sQuery(id+"F0.wireOp",EDGE,"E161"),sQuery(id+"F0.wireOp",EDGE,"E162"),sQuery(id+"F0.wireOp",EDGE,"E163")])],"isStart":false});
            var sketch = newSketch(context, id + "F5", { "sketchPlane" : qUnion([Q0])});
            skCircle(sketch, "E170", {"center": v(34.7, 54.25) * mm, "radius": 0.47 * mm});
            skCircle(sketch, "E171", {"center": v(40.24, 44.23) * mm, "radius": 0.55 * mm});
            skSolve(sketch);
        }
        {
            var Q0;
            Q0 = qSketchRegion(id + "F5", true);
            var Q1;
            Q1=makeQuery(id+"F5.imprint","IMPRINT",FACE,{"disambiguationData":[TD([[makeQuery(id+"F5.imprint","IMPRINT",EDGE,{"derivedFrom":makeQuery(id+"F4.boolean.opBoolean","COPY",EDGE,{"derivedFrom":makeQuery(id+"F4.opExtrude","CAP_EDGE",EDGE,{"disambiguationData":[OSD([sQuery(id+"F3.wireOp",EDGE,"E169")])],"isStart":true})})}),1.0]])]});
            var Q2;
            Q2=makeQuery(id+"F5.imprint","IMPRINT",FACE,{"disambiguationData":[TD([[makeQuery(id+"F5.imprint","IMPRINT",EDGE,{"derivedFrom":makeQuery(id+"F4.boolean.opBoolean","COPY",EDGE,{"derivedFrom":makeQuery(id+"F4.opExtrude","CAP_EDGE",EDGE,{"disambiguationData":[OSD([sQuery(id+"F3.wireOp",EDGE,"E168")])],"isStart":true})})}),1.0]])]});
            var Q3;
            Q3=makeQuery(id+"F5.imprint","IMPRINT",FACE,{"disambiguationData":[TD([[makeQuery(id+"F5.imprint","IMPRINT",EDGE,{"derivedFrom":makeQuery(id+"F4.boolean.opBoolean","COPY",EDGE,{"derivedFrom":makeQuery(id+"F4.opExtrude","CAP_EDGE",EDGE,{"disambiguationData":[OSD([sQuery(id+"F3.wireOp",EDGE,"E167")])],"isStart":true})})}),1.0]])]});
            var Q4;
            Q4=makeQuery(id+"F5.imprint","IMPRINT",FACE,{"disambiguationData":[TD([[makeQuery(id+"F5.imprint","IMPRINT",EDGE,{"derivedFrom":makeQuery(id+"F4.boolean.opBoolean","COPY",EDGE,{"derivedFrom":makeQuery(id+"F4.opExtrude","CAP_EDGE",EDGE,{"disambiguationData":[OSD([sQuery(id+"F3.wireOp",EDGE,"E165")])],"isStart":true})})}),1.0]])]});
            var Q5;
            Q5=makeQuery(id+"F5.imprint","IMPRINT",FACE,{"disambiguationData":[TD([[makeQuery(id+"F5.imprint","IMPRINT",EDGE,{"derivedFrom":makeQuery(id+"F4.boolean.opBoolean","COPY",EDGE,{"derivedFrom":makeQuery(id+"F4.opExtrude","CAP_EDGE",EDGE,{"disambiguationData":[OSD([sQuery(id+"F3.wireOp",EDGE,"E166")])],"isStart":true})})}),1.0]])]});
            extrude(context, id + "F6", {"entities" : qUnion([Q0, Q1, Q2, Q3, Q4, Q5]), "operationType" : NewBodyOperationType.REMOVE, "oppositeDirection" : true, "depth" : 5.9 * mm, "offsetDistance" : 25 * mm});
        }
        {
            var Q0;
            {var subQ0=sQuery(id+"F0.wireOp",EDGE,"E59");var subQ1=sQuery(id+"F0.wireOp",EDGE,"E58");var subQ2=sQuery(id+"F0.wireOp",EDGE,"E57");Q0=makeQuery(id+"F2.boolean.opBoolean","MERGE",FACE,{"derivedFrom":[makeQuery(id+"F1.opExtrude","SWEPT_FACE",FACE,{"disambiguationData":[OSD([subQ2,subQ1,subQ0])]}),makeQuery(id+"F2.opExtrude","SWEPT_FACE",FACE,{"disambiguationData":[OSD([subQ2,subQ1,subQ0])]})]});}
            var sketch = newSketch(context, id + "F7", { "sketchPlane" : qUnion([Q0])});
            skLineSegment(sketch, "E172", {"start": v(19.4, 1.98) * mm, "end": v(26.19, 1.98) * mm});
            skLineSegment(sketch, "E173", {"start": v(19.4, 1.98) * mm, "end": v(19.4, 18.26) * mm});
            skLineSegment(sketch, "E174", {"start": v(19.4, 18.26) * mm, "end": v(26.19, 18.26) * mm});
            skLineSegment(sketch, "E175", {"start": v(26.19, 18.26) * mm, "end": v(26.19, 1.98) * mm});
            skSolve(sketch);
        }
        {
            var Q0;
            Q0=makeQuery(id+"F7.imprint","IMPRINT",FACE,{"disambiguationData":[TD([[makeQuery(id+"F7.imprint","IMPRINT",EDGE,{"derivedFrom":sQuery(id+"F7.wireOp",EDGE,"E172")}),1.0]])]});
            extrude(context, id + "F8", {"entities" : qUnion([Q0]), "operationType" : NewBodyOperationType.REMOVE, "oppositeDirection" : true, "depth" : 10 * mm, "offsetDistance" : 25 * mm});
        }
        {
            var Q0;
            {var subQ0=sQuery(id+"F0.wireOp",EDGE,"E56");Q0=makeQuery(id+"F2.boolean.opBoolean","MERGE",FACE,{"derivedFrom":[makeQuery(id+"F1.opExtrude","SWEPT_FACE",FACE,{"disambiguationData":[OSD([subQ0])]}),makeQuery(id+"F2.opExtrude","SWEPT_FACE",FACE,{"disambiguationData":[OSD([subQ0])]})]});}
            var sketch = newSketch(context, id + "F9", { "sketchPlane" : qUnion([Q0])});
            skLineSegment(sketch, "E176", {"start": v(26.32, 18.26) * mm, "end": v(28.21, 18.26) * mm});
            skLineSegment(sketch, "E177", {"start": v(28.21, 18.26) * mm, "end": v(28.21, 1.98) * mm});
            skLineSegment(sketch, "E178", {"start": v(28.21, 1.98) * mm, "end": v(26.32, 1.98) * mm});
            skSolve(sketch);
        }
        {
            var Q0;
            Q0 = qSketchRegion(id + "F9", true);
            var Q1;
            Q1=makeQuery(id+"F9.imprint","IMPRINT",FACE,{"disambiguationData":[TD([[makeQuery(id+"F9.imprint","IMPRINT",EDGE,{"derivedFrom":sQuery(id+"F9.wireOp",EDGE,"E176")}),-1.0]])]});
            extrude(context, id + "F10", {"entities" : qUnion([Q0, Q1]), "operationType" : NewBodyOperationType.REMOVE, "oppositeDirection" : true, "depth" : 10 * mm, "offsetDistance" : 25 * mm});
        }
        {
            var Q0;
            {var subQ0=sQuery(id+"F0.wireOp",EDGE,"E95");Q0=makeQuery(id+"F2.boolean.opBoolean","MERGE",FACE,{"derivedFrom":[makeQuery(id+"F1.opExtrude","SWEPT_FACE",FACE,{"disambiguationData":[OSD([subQ0])]}),makeQuery(id+"F2.opExtrude","SWEPT_FACE",FACE,{"disambiguationData":[OSD([subQ0])]})]});}
            extrude(context, id + "F11", {"entities" : qUnion([Q0]), "operationType" : NewBodyOperationType.REMOVE, "oppositeDirection" : true, "depth" : 14.7 * mm, "offsetDistance" : 25 * mm});
        }
        {
            var Q0;
            {var subQ0=sQuery(id+"F0.wireOp",EDGE,"E92");var subQ1=sQuery(id+"F0.wireOp",EDGE,"E91");Q0=makeQuery(id+"F2.boolean.opBoolean","MERGE",FACE,{"derivedFrom":[makeQuery(id+"F1.opExtrude","SWEPT_FACE",FACE,{"disambiguationData":[OSD([subQ1,subQ0])]}),makeQuery(id+"F2.opExtrude","SWEPT_FACE",FACE,{"disambiguationData":[OSD([subQ1,subQ0])]})]});}
            var sketch = newSketch(context, id + "F12", { "sketchPlane" : qUnion([Q0])});
            skLineSegment(sketch, "E179", {"start": v(20.5, -3.27) * mm, "end": v(25.8, -3.27) * mm});
            skLineSegment(sketch, "E180", {"start": v(20.5, -16.3) * mm, "end": v(25.8, -16.3) * mm});
            skSolve(sketch);
        }
        {
            var Q0;
            {var subQ0=sQuery(id+"F12.wireOp",EDGE,"E179");Q0=makeQuery(id+"F12.imprint","IMPRINT",FACE,{"disambiguationData":[TD([[makeQuery(id+"F12.imprint","IMPRINT",EDGE,{"derivedFrom":subQ0}),-1.0]])]});}
            extrude(context, id + "F13", {"entities" : qUnion([Q0]), "operationType" : NewBodyOperationType.REMOVE, "oppositeDirection" : true, "depth" : 10 * mm, "offsetDistance" : 25 * mm});
        }
        {
            var Q0;
            {var subQ0=sQuery(id+"F0.wireOp",EDGE,"E93");Q0=makeQuery(id+"F2.boolean.opBoolean","MERGE",FACE,{"derivedFrom":[makeQuery(id+"F1.opExtrude","SWEPT_FACE",FACE,{"disambiguationData":[OSD([subQ0])]}),makeQuery(id+"F2.opExtrude","SWEPT_FACE",FACE,{"disambiguationData":[OSD([subQ0])]})]});}
            var sketch = newSketch(context, id + "F14", { "sketchPlane" : qUnion([Q0])});
            skLineSegment(sketch, "E181", {"start": v(21.27, -16.3) * mm, "end": v(25.4, -16.3) * mm});
            skLineSegment(sketch, "E182", {"start": v(25.4, -16.3) * mm, "end": v(25.4, -3.27) * mm});
            skLineSegment(sketch, "E183", {"start": v(25.4, -3.27) * mm, "end": v(21.27, -3.27) * mm});
            skSolve(sketch);
        }
        {
            var Q0;
            Q0 = qSketchRegion(id + "F14", true);
            var Q1;
            Q1=makeQuery(id+"F14.imprint","IMPRINT",FACE,{"disambiguationData":[TD([[makeQuery(id+"F14.imprint","IMPRINT",EDGE,{"derivedFrom":sQuery(id+"F14.wireOp",EDGE,"E181")}),1.0]])]});
            extrude(context, id + "F15", {"entities" : qUnion([Q0, Q1]), "operationType" : NewBodyOperationType.REMOVE, "oppositeDirection" : true, "depth" : 10 * mm, "offsetDistance" : 25 * mm});
        }
        {
            var Q0;
            Q0=qCreatedBy(makeId("Right.planeOp"),FACE);
            var sketch = newSketch(context, id + "F16", { "sketchPlane" : qUnion([Q0])});
            skLineSegment(sketch, "E184", {"start": v(-1.67, 22.18) * mm, "end": v(-1.67, 18.98) * mm});
            skLineSegment(sketch, "E185", {"start": v(-1.67, 18.98) * mm, "end": v(-19.66, 18.98) * mm});
            skLineSegment(sketch, "E186", {"start": v(-19.66, 18.98) * mm, "end": v(-19.66, 22.76) * mm});
            skLineSegment(sketch, "E187", {"start": v(-19.66, 22.76) * mm, "end": v(-1.67, 22.18) * mm});
            skSolve(sketch);
        }
        {
            var Q0;
            Q0=makeQuery(id+"F16.imprint","IMPRINT",FACE,{"disambiguationData":[TD([[makeQuery(id+"F16.imprint","IMPRINT",EDGE,{"derivedFrom":sQuery(id+"F16.wireOp",EDGE,"E184")}),-1.0]])]});
            extrude(context, id + "F17", {"entities" : qUnion([Q0]), "operationType" : NewBodyOperationType.REMOVE, "depth" : 15.7 * mm, "offsetDistance" : 25 * mm});
        }
        {
            var Q0;
            Q0=makeQuery(id+"F11.boolean.opBoolean","COPY",FACE,{"derivedFrom":makeQuery(id+"F11.opExtrude","CAP_FACE",FACE,{"disambiguationData":[OSD([sQuery(id+"F0.wireOp",EDGE,"E95")])],"isStart":false})});
            extrude(context, id + "F18", {"entities" : qUnion([Q0]), "operationType" : NewBodyOperationType.REMOVE, "oppositeDirection" : true, "depth" : 6.1 * mm, "offsetDistance" : 25 * mm});
        }
    });
